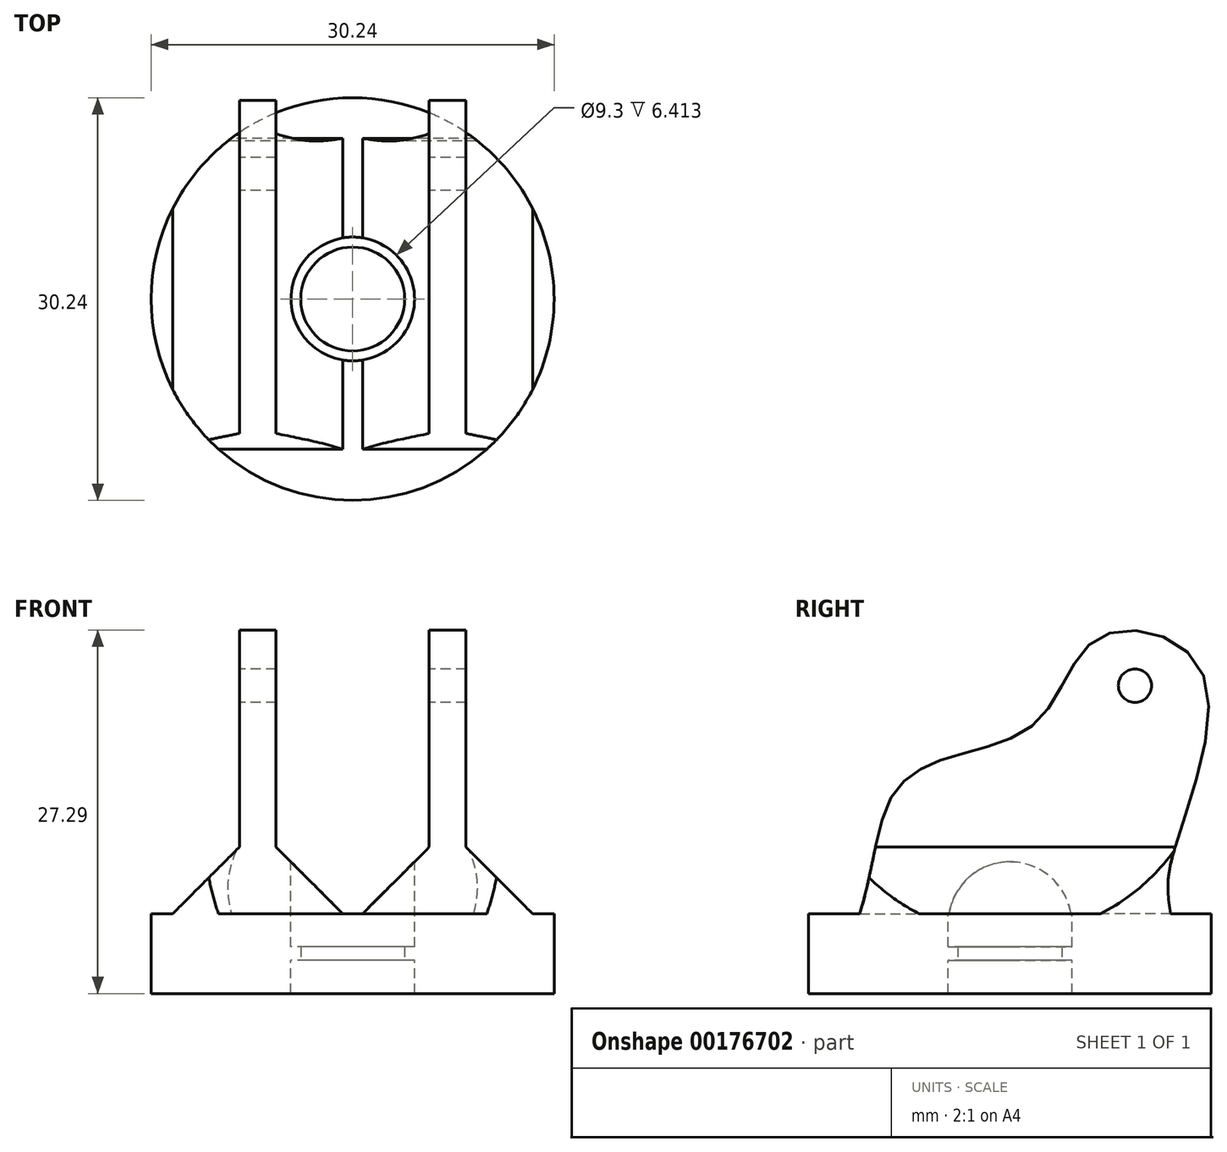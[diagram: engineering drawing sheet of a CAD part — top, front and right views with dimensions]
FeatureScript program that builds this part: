
annotation { "Feature Type Name" : "Feature", "Feature Type Description" : "" }
export const myFeature = defineFeature(function(context is Context, id is Id, definition is map)
    precondition{}
    {
        {
            var Q0;
            Q0=qCreatedBy(makeId("Right.planeOp"),FACE);
            var sketch = newSketch(context, id + "F0", { "sketchPlane" : qUnion([Q0])});
            skFitSpline(sketch, "E0", {"points": [v(-12.5, 0) * mm, v(-9.03, 11.5) * mm, v(-4.66, 14.7) * mm, v(2.26, 17.65) * mm, v(6.84, 23.82) * mm, v(14.43, 21.13) * mm, v(12.09, 6.82) * mm, v(12.5, 0) * mm], "startDerivative": vector(39.23, 73.75) * mm, "endDerivative": vector(9.2, -85.4) * mm});
            skLineSegment(sketch, "E1", {"start": v(12.5, 0) * mm, "end": v(-12.5, 0) * mm});
            skCircle(sketch, "E2", {"center": v(9.39, 20.12) * mm, "radius": 1.25 * mm});
            skSolve(sketch);
        }
        {
            var Q0;
            Q0=qSketchRegion(id+"F0",true);
            extrude(context, id + "F1", {"entities" : qUnion([Q0]), "endBound" : BoundingType.SYMMETRIC, "depth" : 17 * mm});
        }
        {
            var Q0;
            Q0=qSketchRegion(id+"F0",true);
            extrude(context, id + "F2", {"entities" : qUnion([Q0]), "operationType" : NewBodyOperationType.REMOVE, "endBound" : BoundingType.SYMMETRIC, "oppositeDirection" : true, "depth" : 11.5 * mm});
        }
        {
            var Q0;
            Q0=qCreatedBy(makeId("Top.planeOp"),FACE);
            var sketch = newSketch(context, id + "F3", { "sketchPlane" : qUnion([Q0])});
            skCircle(sketch, "E3", {"center": v(0, 0) * mm, "radius": 15.12 * mm});
            skCircle(sketch, "E4", {"center": v(0, 0) * mm, "radius": 4.65 * mm});
            skCircle(sketch, "E5", {"center": v(0, 0) * mm, "radius": 3.9 * mm});
            skSolve(sketch);
        }
        {
            var Q0;
            Q0=qSketchRegion(id+"F3",true);
            extrude(context, id + "F4", {"entities" : qUnion([Q0]), "operationType" : NewBodyOperationType.ADD, "endBound" : BoundingType.SYMMETRIC, "oppositeDirection" : true, "depth" : 6 * mm});
        }
        {
            var Q0;
            Q0=makeQuery(id+"F3.imprint","IMPRINT",FACE,{"disambiguationData":[TD([[makeQuery(id+"F3.imprint","IMPRINT",EDGE,{"derivedFrom":sQuery(id+"F3.wireOp",EDGE,"E4")}),1.0]])]});
            extrude(context, id + "F5", {"entities" : qUnion([Q0]), "operationType" : NewBodyOperationType.ADD, "endBound" : BoundingType.SYMMETRIC, "depth" : 1 * mm});
        }
        {
            var Q0;
            Q0=makeQuery(id+"F4.boolean.opBoolean","INTERSECT",EDGE,{"derivedFrom":[makeQuery(id+"F1.opExtrude","CAP_FACE",FACE,{"disambiguationData":[OSD([sQuery(id+"F0.wireOp",EDGE,"E0"),sQuery(id+"F0.wireOp",EDGE,"E1"),sQuery(id+"F0.wireOp",EDGE,"E2")])],"isStart":false}),makeQuery(id+"F4.opExtrude","CAP_FACE",FACE,{"disambiguationData":[OSD([sQuery(id+"F3.wireOp",EDGE,"E3"),sQuery(id+"F3.wireOp",EDGE,"E4")])],"isStart":true})]});
            var Q1;
            Q1=makeQuery(id+"F4.boolean.opBoolean","INTERSECT",EDGE,{"derivedFrom":[makeQuery(id+"F2.boolean.opBoolean","COPY",FACE,{"derivedFrom":makeQuery(id+"F2.opExtrude","CAP_FACE",FACE,{"disambiguationData":[OSD([sQuery(id+"F0.wireOp",EDGE,"E0"),sQuery(id+"F0.wireOp",EDGE,"E1"),sQuery(id+"F0.wireOp",EDGE,"E2")])],"isStart":true})}),makeQuery(id+"F4.opExtrude","CAP_FACE",FACE,{"disambiguationData":[OSD([sQuery(id+"F3.wireOp",EDGE,"E3"),sQuery(id+"F3.wireOp",EDGE,"E4")])],"isStart":true})]});
            var Q2;
            Q2=makeQuery(id+"F4.boolean.opBoolean","INTERSECT",EDGE,{"derivedFrom":[makeQuery(id+"F2.boolean.opBoolean","COPY",FACE,{"derivedFrom":makeQuery(id+"F2.opExtrude","CAP_FACE",FACE,{"disambiguationData":[OSD([sQuery(id+"F0.wireOp",EDGE,"E0"),sQuery(id+"F0.wireOp",EDGE,"E1"),sQuery(id+"F0.wireOp",EDGE,"E2")])],"isStart":false})}),makeQuery(id+"F4.opExtrude","CAP_FACE",FACE,{"disambiguationData":[OSD([sQuery(id+"F3.wireOp",EDGE,"E3"),sQuery(id+"F3.wireOp",EDGE,"E4")])],"isStart":true})]});
            var Q3;
            Q3=makeQuery(id+"F4.boolean.opBoolean","INTERSECT",EDGE,{"derivedFrom":[makeQuery(id+"F1.opExtrude","CAP_FACE",FACE,{"disambiguationData":[OSD([sQuery(id+"F0.wireOp",EDGE,"E0"),sQuery(id+"F0.wireOp",EDGE,"E1"),sQuery(id+"F0.wireOp",EDGE,"E2")])],"isStart":true}),makeQuery(id+"F4.opExtrude","CAP_FACE",FACE,{"disambiguationData":[OSD([sQuery(id+"F3.wireOp",EDGE,"E3"),sQuery(id+"F3.wireOp",EDGE,"E4")])],"isStart":true})]});
            chamfer(context, id + "F6", {"entities" : qUnion([Q0, Q1, Q2, Q3]), "width" : 5 * mm, "tangentPropagation" : true});
        }
    });
